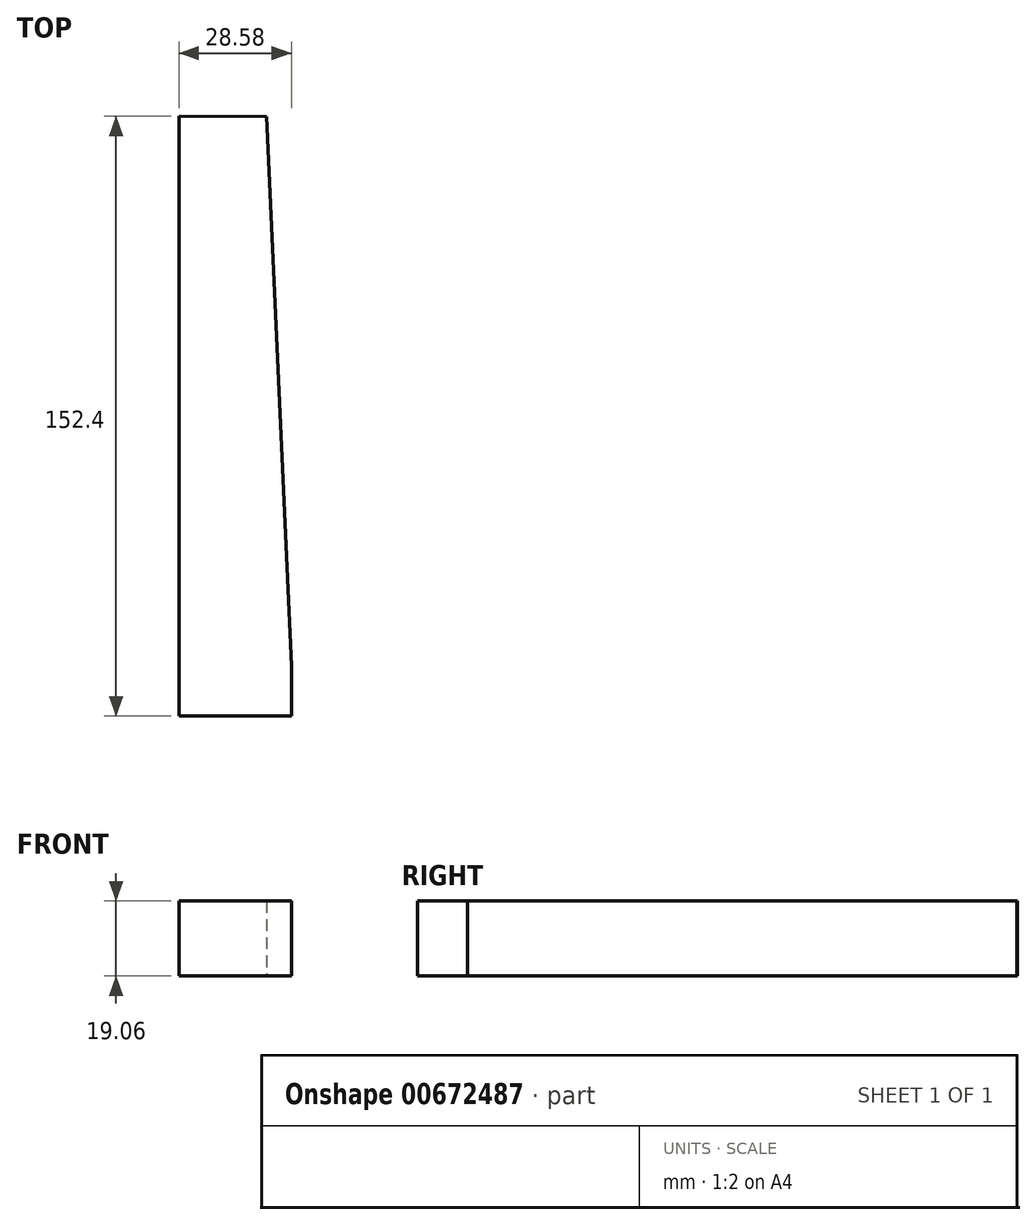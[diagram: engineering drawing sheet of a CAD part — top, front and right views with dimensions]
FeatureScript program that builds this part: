
annotation { "Feature Type Name" : "Feature", "Feature Type Description" : "" }
export const myFeature = defineFeature(function(context is Context, id is Id, definition is map)
    precondition{}
    {
        {
            var Q0;
            Q0=qCreatedBy(makeId("Top.planeOp"),FACE);
            var sketch = newSketch(context, id + "F0", { "sketchPlane" : qUnion([Q0])});
            skLineSegment(sketch, "E0", {"start": v(0, 76.2) * mm, "end": v(0, -76.2) * mm});
            skLineSegment(sketch, "E1", {"start": v(0, -76.2) * mm, "end": v(28.58, -76.2) * mm});
            skLineSegment(sketch, "E2", {"start": v(28.58, -76.2) * mm, "end": v(28.58, -63.5) * mm});
            skLineSegment(sketch, "E3", {"start": v(28.58, -63.5) * mm, "end": v(22.22, 76.13) * mm});
            skLineSegment(sketch, "E4", {"start": v(22.22, 76.13) * mm, "end": v(0, 76.2) * mm});
            skPoint(sketch, "E5", {"position": v(0, 0) * mm});
            skSolve(sketch);
        }
        {
            var Q0;
            Q0=makeQuery(id+"F0.imprint","IMPRINT",FACE,{"disambiguationData":[TD([[makeQuery(id+"F0.imprint","IMPRINT",EDGE,{"derivedFrom":sQuery(id+"F0.wireOp",EDGE,"E0")}),1.0]])]});
            extrude(context, id + "F1", {"entities" : qUnion([Q0]), "depth" : 9.52 * mm, "offsetDistance" : 25.4 * mm, "hasSecondDirection" : true, "secondDirectionOppositeDirection" : true, "secondDirectionDepth" : 9.52 * mm});
        }
    });
